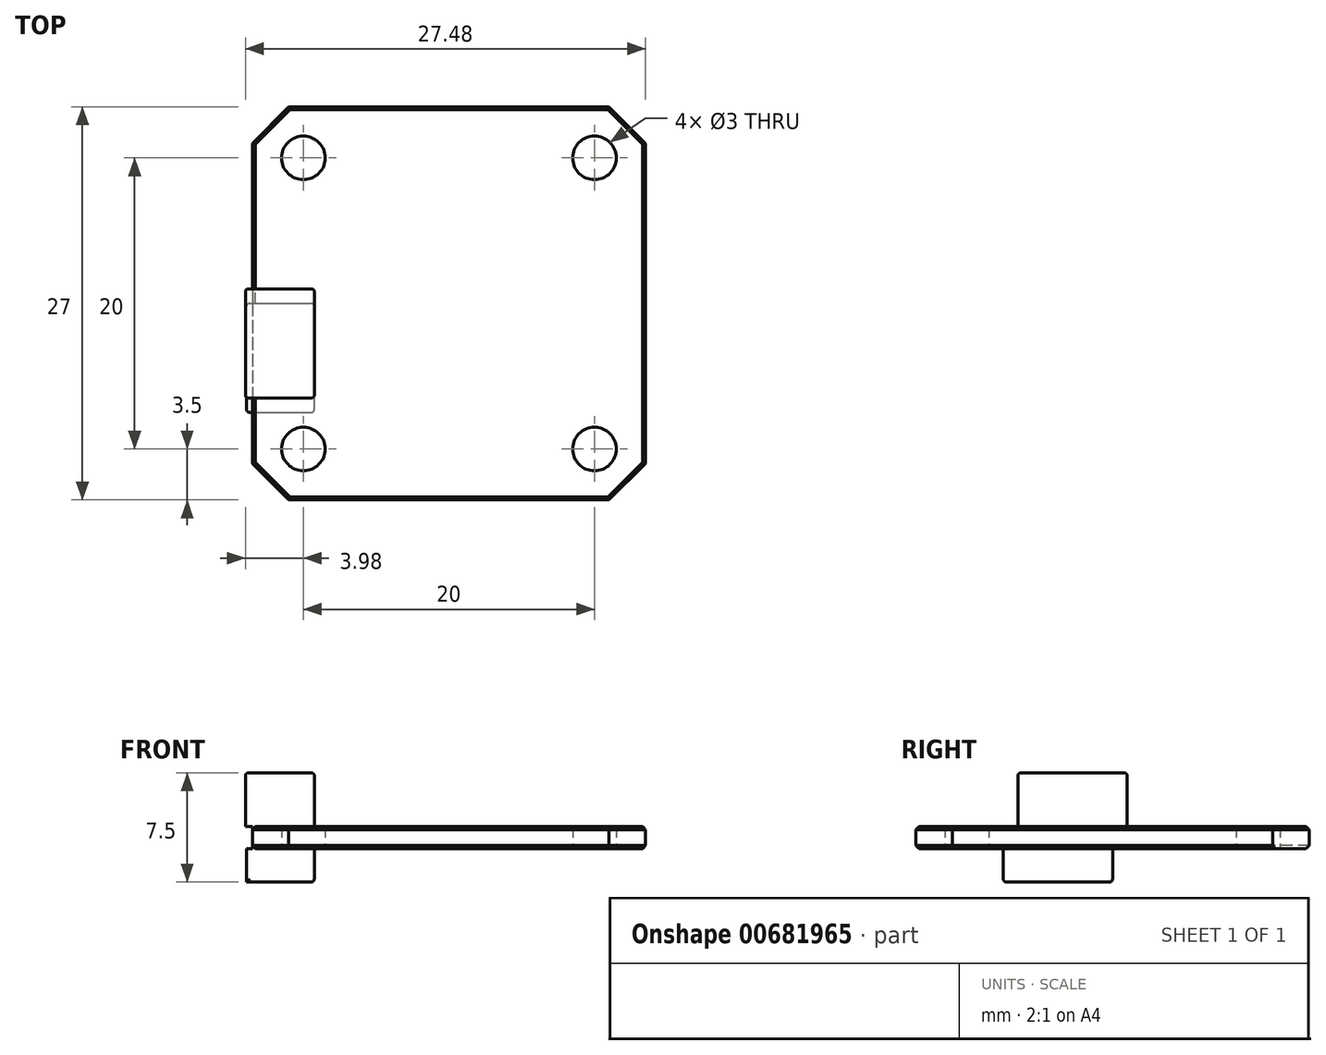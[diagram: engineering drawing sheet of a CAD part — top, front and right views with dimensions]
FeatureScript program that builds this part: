
annotation { "Feature Type Name" : "Feature", "Feature Type Description" : "" }
export const myFeature = defineFeature(function(context is Context, id is Id, definition is map)
    precondition{}
    {
        {
            var Q0;
            Q0=qCreatedBy(makeId("Top.planeOp"),FACE);
            var sketch = newSketch(context, id + "F0", { "sketchPlane" : qUnion([Q0])});
            skPoint(sketch, "E0.0", {"position": v(0, 0) * mm});
            skLineSegment(sketch, "E1.bottom", {"start": v(-11, 13.5) * mm, "end": v(11, 13.5) * mm});
            skLineSegment(sketch, "E1.top", {"start": v(-11, -13.5) * mm, "end": v(11, -13.5) * mm});
            skLineSegment(sketch, "E1.left", {"start": v(-13.5, 11) * mm, "end": v(-13.5, -11) * mm});
            skLineSegment(sketch, "E1.right", {"start": v(13.5, 11) * mm, "end": v(13.5, -11) * mm});
            skLineSegment(sketch, "E2.bottom", {"start": v(-10, 10) * mm, "end": v(10, 10) * mm, "construction": true});
            skLineSegment(sketch, "E2.top", {"start": v(-10, -10) * mm, "end": v(10, -10) * mm, "construction": true});
            skLineSegment(sketch, "E2.left", {"start": v(-10, 10) * mm, "end": v(-10, -10) * mm, "construction": true});
            skLineSegment(sketch, "E2.right", {"start": v(10, 10) * mm, "end": v(10, -10) * mm, "construction": true});
            skCircle(sketch, "E3", {"center": v(-10, 10) * mm, "radius": 1.5 * mm});
            skCircle(sketch, "E4", {"center": v(10, 10) * mm, "radius": 1.5 * mm});
            skCircle(sketch, "E5", {"center": v(10, -10) * mm, "radius": 1.5 * mm});
            skCircle(sketch, "E6", {"center": v(-10, -10) * mm, "radius": 1.5 * mm});
            skLineSegment(sketch, "E7.bottom", {"start": v(11, 13.5) * mm, "end": v(13.5, 11) * mm});
            skLineSegment(sketch, "E7.top", {"start": v(-13.5, -11) * mm, "end": v(-11, -13.5) * mm});
            skLineSegment(sketch, "E7.left", {"start": v(-11, 13.5) * mm, "end": v(-13.5, 11) * mm});
            skLineSegment(sketch, "E7.right", {"start": v(13.5, -11) * mm, "end": v(11, -13.5) * mm});
            skPoint(sketch, "E8.orphan", {"position": v(-13.5, 13.5) * mm});
            skPoint(sketch, "E9.orphan", {"position": v(13.5, 13.5) * mm});
            skPoint(sketch, "E10.orphan", {"position": v(13.5, -13.5) * mm});
            skPoint(sketch, "E11.orphan", {"position": v(-13.5, -13.5) * mm});
            skSolve(sketch);
        }
        {
            var Q0;
            Q0=makeQuery(id+"F0.imprint","IMPRINT",FACE,{"disambiguationData":[TD([[makeQuery(id+"F0.imprint","IMPRINT",EDGE,{"derivedFrom":sQuery(id+"F0.wireOp",EDGE,"E1.bottom")}),-1.0]])]});
            extrude(context, id + "F1", {"entities" : qUnion([Q0]), "depth" : 1.5 * mm, "offsetDistance" : 25 * mm});
        }
        {
            var Q0;
            Q0=makeQuery(id+"F1.opExtrude","CAP_FACE",FACE,{"disambiguationData":[OSD([sQuery(id+"F0.wireOp",EDGE,"E1.bottom"),sQuery(id+"F0.wireOp",EDGE,"E1.top"),sQuery(id+"F0.wireOp",EDGE,"E1.left"),sQuery(id+"F0.wireOp",EDGE,"E1.right"),sQuery(id+"F0.wireOp",EDGE,"E3"),sQuery(id+"F0.wireOp",EDGE,"E4"),sQuery(id+"F0.wireOp",EDGE,"E5"),sQuery(id+"F0.wireOp",EDGE,"E6"),sQuery(id+"F0.wireOp",EDGE,"E7.bottom"),sQuery(id+"F0.wireOp",EDGE,"E7.top"),sQuery(id+"F0.wireOp",EDGE,"E7.left"),sQuery(id+"F0.wireOp",EDGE,"E7.right")])],"isStart":false});
            var sketch = newSketch(context, id + "F2", { "sketchPlane" : qUnion([Q0])});
            skLineSegment(sketch, "E12.bottom", {"start": v(-13.98, 1) * mm, "end": v(-9.24, 1) * mm});
            skLineSegment(sketch, "E12.top", {"start": v(-13.98, -6.5) * mm, "end": v(-9.24, -6.5) * mm});
            skLineSegment(sketch, "E12.left", {"start": v(-13.98, 1) * mm, "end": v(-13.98, -6.5) * mm});
            skLineSegment(sketch, "E12.right", {"start": v(-9.24, 1) * mm, "end": v(-9.24, -6.5) * mm});
            skSolve(sketch);
        }
        {
            var Q0;
            Q0=qSketchRegion(id+"F2",true);
            extrude(context, id + "F3", {"entities" : qUnion([Q0]), "operationType" : NewBodyOperationType.ADD, "depth" : 3.7 * mm, "offsetDistance" : 25 * mm});
        }
        {
            var Q0;
            Q0=makeQuery(id+"F1.opExtrude","CAP_FACE",FACE,{"disambiguationData":[OSD([sQuery(id+"F0.wireOp",EDGE,"E1.bottom"),sQuery(id+"F0.wireOp",EDGE,"E1.top"),sQuery(id+"F0.wireOp",EDGE,"E1.left"),sQuery(id+"F0.wireOp",EDGE,"E1.right"),sQuery(id+"F0.wireOp",EDGE,"E3"),sQuery(id+"F0.wireOp",EDGE,"E4"),sQuery(id+"F0.wireOp",EDGE,"E5"),sQuery(id+"F0.wireOp",EDGE,"E6"),sQuery(id+"F0.wireOp",EDGE,"E7.bottom"),sQuery(id+"F0.wireOp",EDGE,"E7.top"),sQuery(id+"F0.wireOp",EDGE,"E7.left"),sQuery(id+"F0.wireOp",EDGE,"E7.right")])],"isStart":true});
            var sketch = newSketch(context, id + "F4", { "sketchPlane" : qUnion([Q0])});
            skLineSegment(sketch, "E13.bottom", {"start": v(-13.9, 7.5) * mm, "end": v(-9.25, 7.5) * mm});
            skLineSegment(sketch, "E13.top", {"start": v(-13.9, 0) * mm, "end": v(-9.25, 0) * mm});
            skLineSegment(sketch, "E13.left", {"start": v(-13.9, 7.5) * mm, "end": v(-13.9, 0) * mm});
            skLineSegment(sketch, "E13.right", {"start": v(-9.25, 7.5) * mm, "end": v(-9.25, 0) * mm});
            skSolve(sketch);
        }
        {
            var Q0;
            Q0=qSketchRegion(id+"F4",true);
            extrude(context, id + "F5", {"entities" : qUnion([Q0]), "operationType" : NewBodyOperationType.ADD, "depth" : 2.3 * mm, "offsetDistance" : 25 * mm});
        }
        {
            var Q0;
            Q0=makeQuery(id+"F3.opExtrude","CAP_EDGE",EDGE,{"disambiguationData":[OSD([sQuery(id+"F2.wireOp",EDGE,"E12.bottom")])],"isStart":false});
            var Q1;
            Q1=makeQuery(id+"F3.opExtrude","CAP_EDGE",EDGE,{"disambiguationData":[OSD([sQuery(id+"F2.wireOp",EDGE,"E12.right")])],"isStart":false});
            var Q2;
            Q2=makeQuery(id+"F3.opExtrude","CAP_EDGE",EDGE,{"disambiguationData":[OSD([sQuery(id+"F2.wireOp",EDGE,"E12.top")])],"isStart":false});
            var Q3;
            Q3=makeQuery(id+"F3.opExtrude","SWEPT_EDGE",EDGE,{"disambiguationData":[OSD([sQuery(id+"F2.wireOp",EDGE,"E12.top"),sQuery(id+"F2.wireOp",EDGE,"E12.right")])]});
            var Q4;
            Q4=makeQuery(id+"F3.opExtrude","SWEPT_EDGE",EDGE,{"disambiguationData":[OSD([sQuery(id+"F2.wireOp",EDGE,"E12.bottom"),sQuery(id+"F2.wireOp",EDGE,"E12.right")])]});
            var Q5;
            Q5=makeQuery(id+"F3.opExtrude","CAP_EDGE",EDGE,{"disambiguationData":[OSD([sQuery(id+"F2.wireOp",EDGE,"E12.left")])],"isStart":false});
            var Q6;
            Q6=makeQuery(id+"F3.opExtrude","SWEPT_EDGE",EDGE,{"disambiguationData":[OSD([sQuery(id+"F2.wireOp",EDGE,"E12.top"),sQuery(id+"F2.wireOp",EDGE,"E12.left")])]});
            var Q7;
            Q7=makeQuery(id+"F3.opExtrude","SWEPT_EDGE",EDGE,{"disambiguationData":[OSD([sQuery(id+"F2.wireOp",EDGE,"E12.bottom"),sQuery(id+"F2.wireOp",EDGE,"E12.left")])]});
            fillet(context, id + "F6", {"entities" : qUnion([Q0, Q1, Q2, Q3, Q4, Q5, Q6, Q7]), "radius" : .2 * mm, "tangentPropagation" : true, "allowEdgeOverflow" : false});
        }
        {
            var Q0;
            Q0=makeQuery(id+"F1.opExtrude","CAP_EDGE",EDGE,{"disambiguationData":[OSD([sQuery(id+"F0.wireOp",EDGE,"E1.top")])],"isStart":false});
            var Q1;
            Q1=makeQuery(id+"F1.opExtrude","CAP_EDGE",EDGE,{"disambiguationData":[OSD([sQuery(id+"F0.wireOp",EDGE,"E7.top")])],"isStart":false});
            var Q2;
            {var subQ0=sQuery(id+"F0.wireOp",EDGE,"E7.top");var subQ2=sQuery(id+"F0.wireOp",EDGE,"E1.left");var subQ3=makeQuery(id+"F1.opExtrude","CAP_FACE",FACE,{"disambiguationData":[OSD([sQuery(id+"F0.wireOp",EDGE,"E1.bottom"),sQuery(id+"F0.wireOp",EDGE,"E1.top"),subQ2,sQuery(id+"F0.wireOp",EDGE,"E1.right"),sQuery(id+"F0.wireOp",EDGE,"E3"),sQuery(id+"F0.wireOp",EDGE,"E4"),sQuery(id+"F0.wireOp",EDGE,"E5"),sQuery(id+"F0.wireOp",EDGE,"E6"),sQuery(id+"F0.wireOp",EDGE,"E7.bottom"),subQ0,sQuery(id+"F0.wireOp",EDGE,"E7.left"),sQuery(id+"F0.wireOp",EDGE,"E7.right")])],"isStart":false});var subQ4=makeQuery(id+"F1.opExtrude","SWEPT_FACE",FACE,{"disambiguationData":[OSD([subQ2])]});Q2=makeQuery(id+"F3.boolean.opBoolean","SPLIT",EDGE,{"disambiguationData":[topologyDisambiguationEdgeConnected([subQ3,subQ4]),TD([makeQuery(id+"F1.opExtrude","SWEPT_FACE",FACE,{"disambiguationData":[OSD([subQ0])]})])],"derivedFrom":makeQuery(id+"F1.opExtrude","CAP_EDGE",EDGE,{"disambiguationData":[OSD([subQ2])],"isStart":false})});}
            var Q3;
            Q3=makeQuery(id+"F1.opExtrude","CAP_EDGE",EDGE,{"disambiguationData":[OSD([sQuery(id+"F0.wireOp",EDGE,"E7.right")])],"isStart":false});
            var Q4;
            Q4=makeQuery(id+"F1.opExtrude","CAP_EDGE",EDGE,{"disambiguationData":[OSD([sQuery(id+"F0.wireOp",EDGE,"E1.right")])],"isStart":false});
            var Q5;
            {var subQ1=sQuery(id+"F0.wireOp",EDGE,"E7.left");var subQ2=sQuery(id+"F0.wireOp",EDGE,"E1.left");var subQ3=makeQuery(id+"F1.opExtrude","SWEPT_FACE",FACE,{"disambiguationData":[OSD([subQ2])]});var subQ4=makeQuery(id+"F1.opExtrude","CAP_FACE",FACE,{"disambiguationData":[OSD([sQuery(id+"F0.wireOp",EDGE,"E1.bottom"),sQuery(id+"F0.wireOp",EDGE,"E1.top"),subQ2,sQuery(id+"F0.wireOp",EDGE,"E1.right"),sQuery(id+"F0.wireOp",EDGE,"E3"),sQuery(id+"F0.wireOp",EDGE,"E4"),sQuery(id+"F0.wireOp",EDGE,"E5"),sQuery(id+"F0.wireOp",EDGE,"E6"),sQuery(id+"F0.wireOp",EDGE,"E7.bottom"),sQuery(id+"F0.wireOp",EDGE,"E7.top"),subQ1,sQuery(id+"F0.wireOp",EDGE,"E7.right")])],"isStart":false});Q5=makeQuery(id+"F3.boolean.opBoolean","SPLIT",EDGE,{"disambiguationData":[topologyDisambiguationEdgeConnected([subQ4,subQ3]),TD([makeQuery(id+"F1.opExtrude","SWEPT_FACE",FACE,{"disambiguationData":[OSD([subQ1])]})])],"derivedFrom":makeQuery(id+"F1.opExtrude","CAP_EDGE",EDGE,{"disambiguationData":[OSD([subQ2])],"isStart":false})});}
            var Q6;
            Q6=makeQuery(id+"F1.opExtrude","CAP_EDGE",EDGE,{"disambiguationData":[OSD([sQuery(id+"F0.wireOp",EDGE,"E7.left")])],"isStart":false});
            var Q7;
            Q7=makeQuery(id+"F1.opExtrude","CAP_EDGE",EDGE,{"disambiguationData":[OSD([sQuery(id+"F0.wireOp",EDGE,"E1.bottom")])],"isStart":false});
            var Q8;
            Q8=makeQuery(id+"F1.opExtrude","CAP_EDGE",EDGE,{"disambiguationData":[OSD([sQuery(id+"F0.wireOp",EDGE,"E7.bottom")])],"isStart":false});
            var Q9;
            Q9=makeQuery(id+"F1.opExtrude","CAP_EDGE",EDGE,{"disambiguationData":[OSD([sQuery(id+"F0.wireOp",EDGE,"E1.right")])],"isStart":true});
            var Q10;
            Q10=makeQuery(id+"F1.opExtrude","CAP_EDGE",EDGE,{"disambiguationData":[OSD([sQuery(id+"F0.wireOp",EDGE,"E1.bottom")])],"isStart":true});
            var Q11;
            Q11=makeQuery(id+"F1.opExtrude","CAP_EDGE",EDGE,{"disambiguationData":[OSD([sQuery(id+"F0.wireOp",EDGE,"E7.left")])],"isStart":true});
            var Q12;
            {var subQ1=sQuery(id+"F0.wireOp",EDGE,"E7.left");var subQ2=sQuery(id+"F0.wireOp",EDGE,"E1.left");var subQ3=makeQuery(id+"F1.opExtrude","CAP_FACE",FACE,{"disambiguationData":[OSD([sQuery(id+"F0.wireOp",EDGE,"E1.bottom"),sQuery(id+"F0.wireOp",EDGE,"E1.top"),subQ2,sQuery(id+"F0.wireOp",EDGE,"E1.right"),sQuery(id+"F0.wireOp",EDGE,"E3"),sQuery(id+"F0.wireOp",EDGE,"E4"),sQuery(id+"F0.wireOp",EDGE,"E5"),sQuery(id+"F0.wireOp",EDGE,"E6"),sQuery(id+"F0.wireOp",EDGE,"E7.bottom"),sQuery(id+"F0.wireOp",EDGE,"E7.top"),subQ1,sQuery(id+"F0.wireOp",EDGE,"E7.right")])],"isStart":true});var subQ4=makeQuery(id+"F1.opExtrude","SWEPT_FACE",FACE,{"disambiguationData":[OSD([subQ2])]});Q12=makeQuery(id+"F5.boolean.opBoolean","SPLIT",EDGE,{"disambiguationData":[topologyDisambiguationEdgeConnected([subQ3,subQ4]),TD([makeQuery(id+"F1.opExtrude","SWEPT_FACE",FACE,{"disambiguationData":[OSD([subQ1])]})])],"derivedFrom":makeQuery(id+"F1.opExtrude","CAP_EDGE",EDGE,{"disambiguationData":[OSD([subQ2])],"isStart":true})});}
            var Q13;
            {var subQ1=sQuery(id+"F0.wireOp",EDGE,"E1.left");var subQ2=makeQuery(id+"F1.opExtrude","SWEPT_FACE",FACE,{"disambiguationData":[OSD([subQ1])]});var subQ3=sQuery(id+"F0.wireOp",EDGE,"E7.top");var subQ4=makeQuery(id+"F1.opExtrude","CAP_FACE",FACE,{"disambiguationData":[OSD([sQuery(id+"F0.wireOp",EDGE,"E1.bottom"),sQuery(id+"F0.wireOp",EDGE,"E1.top"),subQ1,sQuery(id+"F0.wireOp",EDGE,"E1.right"),sQuery(id+"F0.wireOp",EDGE,"E3"),sQuery(id+"F0.wireOp",EDGE,"E4"),sQuery(id+"F0.wireOp",EDGE,"E5"),sQuery(id+"F0.wireOp",EDGE,"E6"),sQuery(id+"F0.wireOp",EDGE,"E7.bottom"),subQ3,sQuery(id+"F0.wireOp",EDGE,"E7.left"),sQuery(id+"F0.wireOp",EDGE,"E7.right")])],"isStart":true});Q13=makeQuery(id+"F5.boolean.opBoolean","SPLIT",EDGE,{"disambiguationData":[topologyDisambiguationEdgeConnected([subQ4,subQ2]),TD([makeQuery(id+"F1.opExtrude","SWEPT_FACE",FACE,{"disambiguationData":[OSD([subQ3])]})])],"derivedFrom":makeQuery(id+"F1.opExtrude","CAP_EDGE",EDGE,{"disambiguationData":[OSD([subQ1])],"isStart":true})});}
            var Q14;
            Q14=makeQuery(id+"F1.opExtrude","CAP_EDGE",EDGE,{"disambiguationData":[OSD([sQuery(id+"F0.wireOp",EDGE,"E7.top")])],"isStart":true});
            var Q15;
            Q15=makeQuery(id+"F1.opExtrude","CAP_EDGE",EDGE,{"disambiguationData":[OSD([sQuery(id+"F0.wireOp",EDGE,"E1.top")])],"isStart":true});
            var Q16;
            Q16=makeQuery(id+"F1.opExtrude","CAP_EDGE",EDGE,{"disambiguationData":[OSD([sQuery(id+"F0.wireOp",EDGE,"E7.right")])],"isStart":true});
            chamfer(context, id + "F7", {"entities" : qUnion([Q0, Q1, Q2, Q3, Q4, Q5, Q6, Q7, Q8, Q9, Q10, Q11, Q12, Q13, Q14, Q15, Q16]), "width" : .2 * mm, "tangentPropagation" : true});
        }
        {
            var Q0;
            Q0=makeQuery(id+"F5.opExtrude","CAP_EDGE",EDGE,{"disambiguationData":[OSD([sQuery(id+"F4.wireOp",EDGE,"E13.bottom")])],"isStart":false});
            var Q1;
            Q1=makeQuery(id+"F5.opExtrude","CAP_EDGE",EDGE,{"disambiguationData":[OSD([sQuery(id+"F4.wireOp",EDGE,"E13.right")])],"isStart":false});
            var Q2;
            Q2=makeQuery(id+"F5.opExtrude","CAP_EDGE",EDGE,{"disambiguationData":[OSD([sQuery(id+"F4.wireOp",EDGE,"E13.top")])],"isStart":false});
            var Q3;
            Q3=makeQuery(id+"F5.opExtrude","SWEPT_EDGE",EDGE,{"disambiguationData":[OSD([sQuery(id+"F4.wireOp",EDGE,"E13.top"),sQuery(id+"F4.wireOp",EDGE,"E13.left")])]});
            var Q4;
            Q4=makeQuery(id+"F5.opExtrude","SWEPT_EDGE",EDGE,{"disambiguationData":[OSD([sQuery(id+"F4.wireOp",EDGE,"E13.bottom"),sQuery(id+"F4.wireOp",EDGE,"E13.left")])]});
            var Q5;
            Q5=makeQuery(id+"F5.opExtrude","SWEPT_EDGE",EDGE,{"disambiguationData":[OSD([sQuery(id+"F4.wireOp",EDGE,"E13.bottom"),sQuery(id+"F4.wireOp",EDGE,"E13.right")])]});
            var Q6;
            Q6=makeQuery(id+"F5.opExtrude","SWEPT_EDGE",EDGE,{"disambiguationData":[OSD([sQuery(id+"F4.wireOp",EDGE,"E13.top"),sQuery(id+"F4.wireOp",EDGE,"E13.right")])]});
            fillet(context, id + "F8", {"entities" : qUnion([Q0, Q1, Q2, Q3, Q4, Q5, Q6]), "radius" : .2 * mm, "tangentPropagation" : true, "allowEdgeOverflow" : false});
        }
    });
